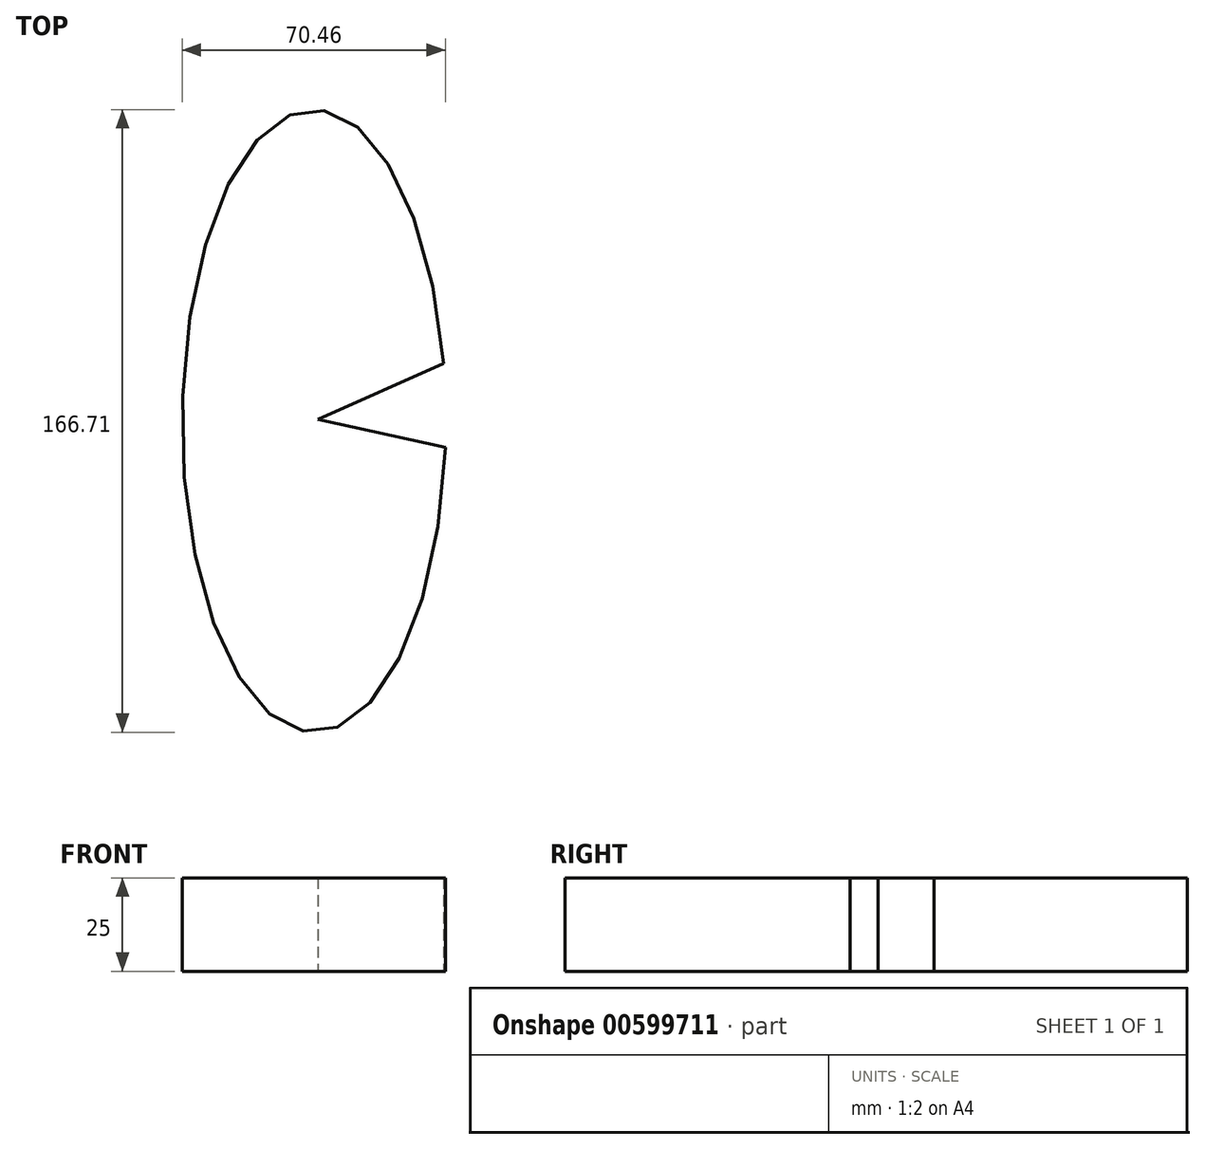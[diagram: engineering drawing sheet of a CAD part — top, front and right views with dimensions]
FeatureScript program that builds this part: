
annotation { "Feature Type Name" : "Feature", "Feature Type Description" : "" }
export const myFeature = defineFeature(function(context is Context, id is Id, definition is map)
    precondition{}
    {
        {
            var Q0;
            Q0=qCreatedBy(makeId("Top.planeOp"),FACE);
            var sketch = newSketch(context, id + "F0", { "sketchPlane" : qUnion([Q0])});
            skEllipse(sketch, "E0", {"center": v(-106.74, -41.59) * mm, "majorRadius": 83.35 * mm, "minorRadius": 35.29 * mm, "majorAxis": v(0, -1)});
            skSolve(sketch);
        }
        {
            var Q0;
            Q0 = qSketchRegion(id + "F0", true);
            var sketch = newSketch(context, id + "F1", { "sketchPlane" : qUnion([Q0])});
            skLineSegment(sketch, "E1", {"start": v(-57.32, -51.72) * mm, "end": v(-105.68, -41.1) * mm});
            skLineSegment(sketch, "E2", {"start": v(-105.68, -41.1) * mm, "end": v(-57.32, -19.55) * mm});
            skLineSegment(sketch, "E3", {"start": v(-57.32, -19.55) * mm, "end": v(-57.32, -51.72) * mm});
            skSolve(sketch);
        }
        {
            var Q0;
            {var subQ0=sQuery(id+"F1.wireOp",EDGE,"E2");var subQ1=sQuery(id+"F1.wireOp",EDGE,"E1");var subQ2=makeQuery(id+"F1.imprint","INTERSECT",VERTEX,{"derivedFrom":[subQ1,subQ0]});Q0=makeQuery(id+"F1.imprint","IMPRINT",FACE,{"disambiguationData":[TD([[makeQuery(id+"F1.imprint","IMPRINT",EDGE,{"disambiguationData":[TD([[subQ2,1.0]])],"derivedFrom":subQ1}),1.0]])]});}
            extrude(context, id + "F2", {"entities" : qUnion([Q0]), "depth" : 25 * mm, "offsetDistance" : 25 * mm});
        }
    });
